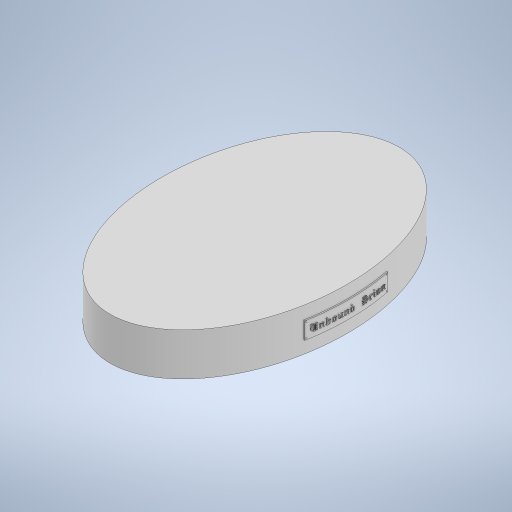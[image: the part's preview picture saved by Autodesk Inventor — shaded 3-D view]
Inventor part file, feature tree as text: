
AUTODESK INVENTOR PART (.ipt)
format: ipt  version: 2024 (Build 280153000, 153)  size: 1,915,904 bytes
history: native  units: mm
features: split x27, thicken_offset x19, sketch x4, extrude x2, plane x1, fillet x1, other x1
ambient origin geometry x8: Origin, YZ Plane, XZ Plane, XY Plane, X Axis, Y Axis, Z Axis, Center Point
bodies: Solid1 (feature_tree)
feature tree (55):
  extrude  "Extrusion1"  Depth=54.5mm
  extrude  "Extrusion2"  Depth=51.0mm
  plane  "Work Plane2"
  sketch  "Sketch4"  dims[d6=3.0mm d7=0.0mm d9=80.0mm d10=32.748225mm d13=5.920965mm d14=10.0mm d16=49.0mm d18=0.75mm d19=0.75mm d20=0.75mm d21=0.75mm d22=0.75mm d23=0.75mm d25=0.75mm d26=0.75mm d27=0.75mm d28=0.75mm d29=0.75mm d30=0.75mm d31=0.5mm d32=0.5mm d33=0.5mm d34=0.5mm d35=0.5mm d36=0.5mm d37=0.5mm d38=0.5mm d39=0.5mm d40=0.5mm d41=0.5mm d42=0.5mm d43=0.5mm d44=0.5mm d45=0.5mm d46=0.5mm d47=0.5mm d48=0.5mm d49=0.5mm d50=0.5mm d51=0.5mm d52=0.5mm d53=0.5mm d54=0.5mm d55=0.5mm d56=0.5mm d57=0.5mm d58=0.5mm d59=0.4mm d60=0.4mm d61=0.4mm d62=0.4mm d63=0.4mm d64=0.4mm d65=0.4mm d66=0.4mm d67=0.35mm]
  sketch  "3D Sketch1"
  split  "Split1"
  split  "Split2"
  split  "Split3"
  split  "Split4"
  split  "Split5"
  split  "Split6"
  split  "Split7"
  split  "Split8"
  split  "Split9"
  split  "Split10"
  split  "Split11"
  split  "Split12"
  split  "Split13"
  split  "Split14"
  split  "Split15"
  split  "Split16"
  split  "Split17"
  split  "Split18"
  split  "Split19"
  split  "Split20"
  split  "Split21"
  split  "Split22"
  split  "Split23"
  split  "Split24"
  split  "Split25"
  split  "Split26"
  split  "Split27"
  thicken_offset  "Thicken1"
  thicken_offset  "Thicken2"
  thicken_offset  "Thicken3"
  thicken_offset  "Thicken4"
  thicken_offset  "Thicken5"
  thicken_offset  "Thicken6"
  thicken_offset  "Thicken7"
  thicken_offset  "Thicken8"
  thicken_offset  "Thicken9"
  thicken_offset  "Thicken10"
  thicken_offset  "Thicken11"
  thicken_offset  "Thicken12"
  thicken_offset  "Thicken13"
  thicken_offset  "Thicken14"
  thicken_offset  "Thicken15"
  thicken_offset  "Thicken16"
  thicken_offset  "Thicken17"
  thicken_offset  "Thicken18"
  thicken_offset  "Thicken19"
  fillet  "Fillet1"  Radius=22.0mm
  sketch  "Sketch1"  dims[d0=85.0mm d1=54.5mm]
  sketch  "Sketch2"  dims[d2=81.5mm d3=51.0mm d4=22.0mm d5=0.0mm]
  other  "Project to Surface1"
